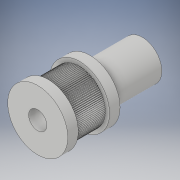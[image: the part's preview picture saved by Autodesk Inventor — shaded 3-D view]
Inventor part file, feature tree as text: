
AUTODESK INVENTOR PART (.ipt)
format: ipt  version: 2019 (Build 230136000, 136)  size: 547,840 bytes
history: native  units: mm
features: extrude x5, sketch x5, pattern_circular x1, plane x1, mirror x1
ambient origin geometry x8: Origin, YZ Plane, XZ Plane, XY Plane, X Axis, Y Axis, Z Axis, Center Point
bodies: Solid1 (feature_tree)
feature tree (13):
  extrude  "Extrusion1"  Depth=20.0mm TaperAngle=0.0deg
  extrude  "Extrusion2"  TaperAngle=30.0deg  [1 undecoded]
  pattern_circular  "Circular Pattern1"  Count=2  [1 undecoded]
  extrude  "Extrusion3"  Depth=20.0mm TaperAngle=360.0deg
  plane  "Work Plane1"
  mirror  "Mirror1"
  extrude  "Extrusion5"  Depth=20.0mm
  extrude  "Extrusion4"  Depth=4.0mm TaperAngle=0.0deg
  sketch  "Sketch1"  dims[d0=20.0mm d1=20.0mm d2=0.0mm]
  sketch  "Sketch2"  dims[d3=30.0deg d9=30.0deg]
  sketch  "Sketch3"  dims[d10=30.0deg]
  sketch  "Sketch4"  dims[d11=0.5mm]
  sketch  "Sketch5"  dims[d12=0.5mm d13=20.0mm d14=0.0mm d15=1080.0mm d16=360.0deg d18=23.0mm d19=4.0mm d20=0.0mm d21=10.0mm d22=7.0mm d23=40.0mm d24=0.0mm d25=15.0mm d26=20.0mm d27=0.0mm]
note: 2 required parameter values undecoded (feature->parameter linkage not recoverable at this tier; creation-order binding heuristic only, values carry confidence <= 0.55)
